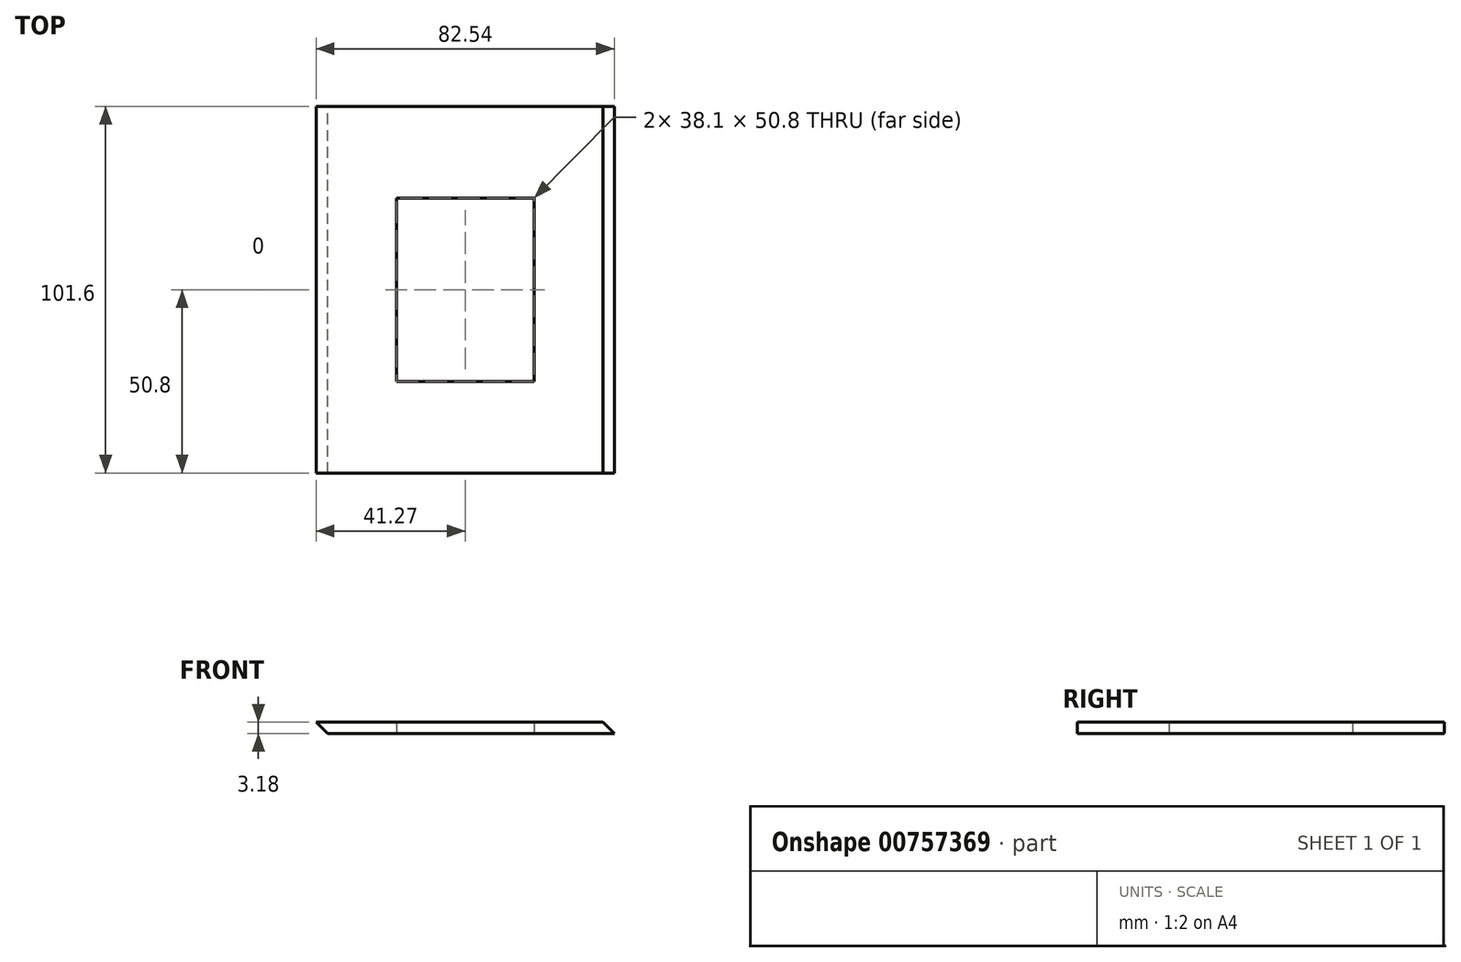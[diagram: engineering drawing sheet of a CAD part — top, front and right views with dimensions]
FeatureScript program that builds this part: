
annotation { "Feature Type Name" : "Feature", "Feature Type Description" : "" }
export const myFeature = defineFeature(function(context is Context, id is Id, definition is map)
    precondition{}
    {
        {
            var Q0;
            Q0=qCreatedBy(makeId("Top.planeOp"),FACE);
            var sketch = newSketch(context, id + "F0", { "sketchPlane" : qUnion([Q0])});
            skLineSegment(sketch, "E0.bottom", {"start": v(-41.28, -50.8) * mm, "end": v(41.28, -50.8) * mm});
            skLineSegment(sketch, "E0.top", {"start": v(-41.27, 50.8) * mm, "end": v(41.28, 50.8) * mm});
            skLineSegment(sketch, "E0.left", {"start": v(-41.28, -50.8) * mm, "end": v(-41.27, 50.8) * mm});
            skLineSegment(sketch, "E0.right", {"start": v(41.28, -50.8) * mm, "end": v(41.28, 50.8) * mm});
            skPoint(sketch, "E0.middle", {"position": v(0, 0) * mm});
            skSolve(sketch);
        }
        {
            var Q0;
            Q0 = qSketchRegion(id + "F0", true);
            extrude(context, id + "F1", {"entities" : qUnion([Q0]), "depth" : 3.17 * mm, "offsetDistance" : 25.4 * mm});
        }
        {
            var Q0;
            Q0=makeQuery(id+"F1.opExtrude","CAP_EDGE",EDGE,{"disambiguationData":[OSD([sQuery(id+"F0.wireOp",EDGE,"E0.left")])],"isStart":true});
            chamfer(context, id + "F2", {"entities" : qUnion([Q0]), "width" : 3.17 * mm, "tangentPropagation" : true});
        }
        {
            var Q0;
            Q0=makeQuery(id+"F1.opExtrude","CAP_FACE",FACE,{"disambiguationData":[OSD([sQuery(id+"F0.wireOp",EDGE,"E0.bottom"),sQuery(id+"F0.wireOp",EDGE,"E0.top"),sQuery(id+"F0.wireOp",EDGE,"E0.left"),sQuery(id+"F0.wireOp",EDGE,"E0.right")])],"isStart":true});
            var sketch = newSketch(context, id + "F3", { "sketchPlane" : qUnion([Q0])});
            skLineSegment(sketch, "E1.bottom", {"start": v(19.05, 25.4) * mm, "end": v(-19.05, 25.4) * mm});
            skLineSegment(sketch, "E1.top", {"start": v(19.05, -25.4) * mm, "end": v(-19.05, -25.4) * mm});
            skLineSegment(sketch, "E1.left", {"start": v(19.05, 25.4) * mm, "end": v(19.05, -25.4) * mm});
            skLineSegment(sketch, "E1.right", {"start": v(-19.05, 25.4) * mm, "end": v(-19.05, -25.4) * mm});
            skPoint(sketch, "E1.middle", {"position": v(0, 0) * mm});
            skSolve(sketch);
        }
        {
            var Q0;
            Q0=makeQuery(id+"F3.imprint","IMPRINT",FACE,{"disambiguationData":[TD([[makeQuery(id+"F3.imprint","IMPRINT",EDGE,{"derivedFrom":sQuery(id+"F3.wireOp",EDGE,"E1.bottom")}),1.0]])]});
            extrude(context, id + "F4", {"entities" : qUnion([Q0]), "operationType" : NewBodyOperationType.REMOVE, "oppositeDirection" : true, "depth" : 3.17 * mm, "offsetDistance" : 25.4 * mm});
        }
        {
            var Q0;
            Q0=makeQuery(id+"F1.opExtrude","CAP_EDGE",EDGE,{"disambiguationData":[OSD([sQuery(id+"F0.wireOp",EDGE,"E0.right")])],"isStart":false});
            chamfer(context, id + "F5", {"entities" : qUnion([Q0]), "width" : 3.17 * mm, "tangentPropagation" : true});
        }
    });
